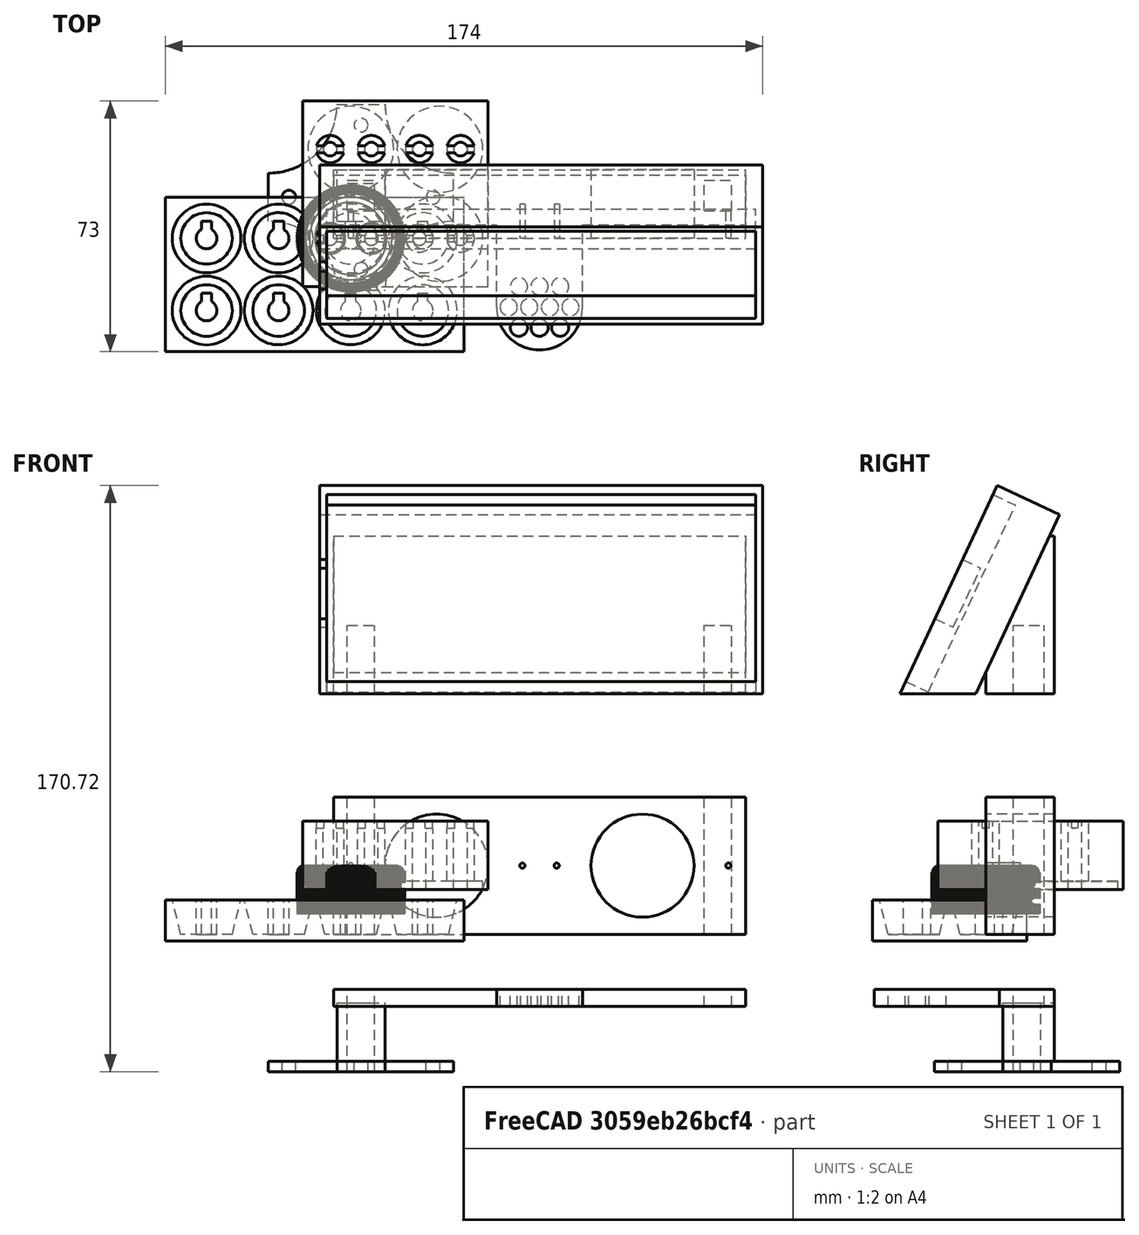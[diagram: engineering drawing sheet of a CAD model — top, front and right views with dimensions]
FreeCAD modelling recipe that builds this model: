
FCSTD DOCUMENT  (FreeCAD 0.14R3703 (Git))
Label: Drinks
License: CC-BY 3.0
LicenseURL: http://creativecommons.org/licenses/by/3.0/
objects: Part::Cylinder×32, Part::Box×22, Part::Cut×21, Part::MultiFuse×19, Part::Feature×2, Part::Cone×1, Mesh::Feature×1
note: 97 computed .brp shape members not serialized (recipe doc carries the construction recipe); baked Part::Feature solids carry a one-line shape summary decoded from their .brp

FEATURE [Part::Box] Box  label="Cube"
  Height = 40
  Length = 120
  Placement = pos=(-5,0,0) rot=(0,0,1;0rad)
  Width = 20
FEATURE [Part::Cylinder] Cylinder  label="Zylinder"
  Angle = 360
  Height = 20
  Placement = pos=(25,20,20) rot=(1,0,0;1.5708rad)
  Radius = 15
FEATURE [Part::Cylinder] Cylinder001  label="Zylinder001"
  Angle = 360
  Height = 10
  Placement = pos=(0,10,20) rot=(1,0,0;1.5708rad)
  Radius = 0.75
FEATURE [Part::Cylinder] Cylinder002  label="Zylinder002"
  Angle = 360
  Height = 10
  Placement = pos=(50,10,20) rot=(1,0,0;1.5708rad)
  Radius = 0.75
FEATURE [Part::MultiFuse] Fusion
  Placement = pos=(60,0,0) rot=(0,0,1;0rad)
  Shapes = -> [Cylinder,Cylinder001,Cylinder002]
FEATURE [Part::MultiFuse] Fusion001
  Shapes = -> [Cylinder,Cylinder001,Cylinder002]
FEATURE [Part::Box] Box001  label="Cube001"
  Height = 40
  Length = 8
  Placement = pos=(-1,8,0) rot=(0,0,1;0rad)
  Width = 9
FEATURE [Part::Box] Box002  label="Cube002"
  Height = 40
  Length = 8
  Placement = pos=(103,8,0) rot=(0,0,1;0rad)
  Width = 9
FEATURE [Part::MultiFuse] Fusion002
  Shapes = -> [Fusion,Fusion001,Box001,Box002]
FEATURE [Part::Cut] Cut  label="MotorHalterung"
  Base = -> Box
  Tool = -> Fusion002
FEATURE [Part::Box] Box003  label="Cube003"
  Height = 67
  Length = 129
  Placement = pos=(-9,-25,70) rot=(-1,0,0;0.436332rad)
  Width = 20
FEATURE [Part::Box] Box004  label="Cube004"
  Height = 20
  Length = 8
  Placement = pos=(-1,8,70) rot=(0,0,1;0rad)
  Width = 9
FEATURE [Part::Box] Box005  label="Cube005"
  Height = 20
  Length = 8
  Placement = pos=(103,8,70) rot=(0,0,1;0rad)
  Width = 9
FEATURE [Part::Box] Box006  label="Cube006"
  Height = 46
  Length = 120
  Placement = pos=(-5,0,70) rot=(0,0,1;0rad)
  Width = 20
FEATURE [Part::Box] Box007  label="Cube007"
  Height = 60
  Length = 125
  Placement = pos=(-7,-24,74) rot=(-1,0,0;0.436332rad)
  Width = 8
FEATURE [Part::Box] Box008  label="Cube008"
  Height = 10
  Length = 129
  Placement = pos=(-9,-27,60) rot=(0,0,1;0rad)
  Width = 47
FEATURE [Part::MultiFuse] Fusion003
  Shapes = -> [Box003,Box006]
FEATURE [Part::MultiFuse] Fusion004
  Shapes = -> [Box004,Box005,Box007,Box008]
FEATURE [Part::Cut] Cut001
  Base = -> Fusion003
  Tool = -> Fusion004
FEATURE [Part::Box] Box009  label="Cube009"
  Height = 19
  Length = 2
  Placement = pos=(-9,-15,92) rot=(-1,0,0;0.436332rad)
  Width = 6
FEATURE [Part::Cut] Cut002  label="iPhoneHalterung"
  Base = -> Cut001
  Tool = -> Box009
FEATURE [Part::Box] Box010  label="Cube010"
  Height = 5
  Length = 8
  Placement = pos=(103,8,0) rot=(0,0,1;0rad)
  Width = 9
FEATURE [Part::Box] Box011  label="Cube011"
  Height = 5
  Length = 8
  Placement = pos=(-1,8,0) rot=(0,0,1;0rad)
  Width = 9
FEATURE [Part::Box] Box012  label="Cube012"
  Height = 5
  Length = 120
  Placement = pos=(-5,4,0) rot=(0,0,1;0rad)
  Width = 16
FEATURE [Part::Cylinder] Cylinder003  label="Zylinder003"
  Angle = 360
  Height = 5
  Placement = pos=(3,0,0) rot=(0,0,1;0rad)
  Radius = 2.5
FEATURE [Part::Cylinder] Cylinder004  label="Zylinder004"
  Angle = 360
  Height = 5
  Placement = pos=(9,0,0) rot=(0,0,1;0rad)
  Radius = 2.5
FEATURE [Part::Cylinder] Cylinder005  label="Zylinder005"
  Angle = 360
  Height = 5
  Placement = pos=(-3,0,0) rot=(0,0,1;0rad)
  Radius = 2.5
FEATURE [Part::Cylinder] Cylinder006  label="Zylinder006"
  Angle = 360
  Height = 5
  Placement = pos=(-9,0,0) rot=(0,0,1;0rad)
  Radius = 2.5
FEATURE [Part::Cylinder] Cylinder007  label="Zylinder007"
  Angle = 360
  Height = 5
  Placement = pos=(-6,6,0) rot=(0,0,1;0rad)
  Radius = 2.5
FEATURE [Part::Cylinder] Cylinder008  label="Zylinder008"
  Angle = 360
  Height = 5
  Placement = pos=(0,6,0) rot=(0,0,1;0rad)
  Radius = 2.5
FEATURE [Part::Cylinder] Cylinder009  label="Zylinder009"
  Angle = 360
  Height = 5
  Placement = pos=(0,-6,0) rot=(0,0,1;0rad)
  Radius = 2.5
FEATURE [Part::Cylinder] Cylinder010  label="Zylinder010"
  Angle = 360
  Height = 5
  Placement = pos=(-6,-6,0) rot=(0,0,1;0rad)
  Radius = 2.5
FEATURE [Part::Cylinder] Cylinder011  label="Zylinder011"
  Angle = 360
  Height = 5
  Placement = pos=(55,-20,0) rot=(0,0,1;0rad)
  Radius = 12.5
FEATURE [Part::Cylinder] Cylinder012  label="Zylinder012"
  Angle = 360
  Height = 5
  Placement = pos=(6,-6,0) rot=(0,0,1;0rad)
  Radius = 2.5
FEATURE [Part::Cylinder] Cylinder013  label="Zylinder013"
  Angle = 360
  Height = 5
  Placement = pos=(6,6,0) rot=(0,0,1;0rad)
  Radius = 2.5
FEATURE [Part::MultiFuse] Fusion005
  Placement = pos=(55,-20,0) rot=(0,0,1;0rad)
  Shapes = -> [Cylinder013,Cylinder012,Cylinder010,Cylinder009,Cylinder008,Cylinder005,Cylinder003,Cylinder004,Cylinder006,Cylinder007]
FEATURE [Part::Box] Box013  label="Cube013"
  Height = 5
  Length = 25
  Placement = pos=(42.5,-20,0) rot=(0,0,1;0rad)
  Width = 26
FEATURE [Part::MultiFuse] Fusion006
  Shapes = -> [Box012,Box013,Cylinder011]
FEATURE [Part::MultiFuse] Fusion007
  Shapes = -> [Fusion005,Box010,Box011]
FEATURE [Part::Cut] Cut003  label="SchlauchHalterung"
  Base = -> Fusion006
  Placement = pos=(0,0,-21) rot=(0,0,1;0rad)
  Tool = -> Fusion007
FEATURE [Part::Box] Box015  label="Cube015"
  Height = 20
  Length = 14
  Placement = pos=(-4,5,-40) rot=(0,0,1;0rad)
  Width = 15
FEATURE [Part::Box] Box016  label="Cube016"
  Height = 20
  Length = 8
  Placement = pos=(-1,8,-40) rot=(0,0,1;0rad)
  Width = 8
FEATURE [Part::Box] Box018  label="Cube018"
  Height = 3
  Length = 54
  Placement = pos=(-24,-15,-40) rot=(0,0,1;0rad)
  Width = 54
FEATURE [Part::Cylinder] Cylinder014  label="Zylinder014"
  Angle = 360
  Height = 3
  Placement = pos=(30,-15,-40) rot=(0,0,1;0rad)
  Radius = 20
FEATURE [Part::Cylinder] Cylinder015  label="Zylinder015"
  Angle = 360
  Height = 3
  Placement = pos=(-24,-15,-40) rot=(0,0,1;0rad)
  Radius = 20
FEATURE [Part::Cylinder] Cylinder016  label="Zylinder016"
  Angle = 360
  Height = 3
  Placement = pos=(-24,39,-40) rot=(0,0,1;0rad)
  Radius = 20
FEATURE [Part::Cylinder] Cylinder017  label="Zylinder017"
  Angle = 360
  Height = 3
  Placement = pos=(30,39,-40) rot=(0,0,1;0rad)
  Radius = 20
FEATURE [Part::Cylinder] Cylinder018  label="Zylinder018"
  Angle = 360
  Height = 3
  Placement = pos=(3,-9,-40) rot=(0,0,1;0rad)
  Radius = 2
FEATURE [Part::Cylinder] Cylinder019  label="Zylinder019"
  Angle = 360
  Height = 3
  Placement = pos=(3,33,-40) rot=(0,0,1;0rad)
  Radius = 2
FEATURE [Part::Cylinder] Cylinder020  label="Zylinder020"
  Angle = 360
  Height = 3
  Placement = pos=(24,12,-40) rot=(0,0,1;0rad)
  Radius = 2
FEATURE [Part::Cylinder] Cylinder021  label="Zylinder021"
  Angle = 360
  Height = 3
  Placement = pos=(-18,12,-40) rot=(0,0,1;0rad)
  Radius = 2
FEATURE [Part::MultiFuse] Fusion008
  Shapes = -> [Box015,Box018]
FEATURE [Part::MultiFuse] Fusion009
  Shapes = -> [Box016,Cylinder018,Cylinder019,Cylinder014,Cylinder021,Cylinder017,Cylinder016,Cylinder015,Cylinder020]
FEATURE [Part::Cut] Cut004  label="Sockel"
  Base = -> Fusion008
  Tool = -> Fusion009
FEATURE [Part::Cone] Cone  label="Kegel"
  Angle = 360
  Height = 10
  Radius1 = 7.5
  Radius2 = 10
FEATURE [Part::Cylinder] Cylinder022  label="Zylinder022"
  Angle = 360
  Height = 10
  Radius = 3
FEATURE [Part::Box] Box019  label="Cube019"
  Height = 10
  Length = 3
  Placement = pos=(-1.5,2,0) rot=(0,0,1;0rad)
  Width = 3
FEATURE [Part::MultiFuse] Fusion010
  Shapes = -> [Cylinder022,Box019]
FEATURE [Part::Cut] Cut005
  Base = -> Cone
  Placement = pos=(21,-21,0) rot=(0,0,1;0rad)
  Tool = -> Fusion010
FEATURE [Part::Cut] Cut006
  Base = -> Cone
  Placement = pos=(0,-21,0) rot=(0,0,1;0rad)
  Tool = -> Fusion010
FEATURE [Part::Cut] Cut007
  Base = -> Cone
  Placement = pos=(-42,-21,0) rot=(0,0,1;0rad)
  Tool = -> Fusion010
FEATURE [Part::Cut] Cut008
  Base = -> Cone
  Placement = pos=(21,0,0) rot=(0,0,1;0rad)
  Tool = -> Fusion010
FEATURE [Part::Cut] Cut009
  Base = -> Cone
  Placement = pos=(-42,0,0) rot=(0,0,1;0rad)
  Tool = -> Fusion010
FEATURE [Part::Cut] Cut010
  Base = -> Cone
  Tool = -> Fusion010
FEATURE [Part::Cut] Cut011
  Base = -> Cone
  Placement = pos=(-21,-21,0) rot=(0,0,1;0rad)
  Tool = -> Fusion010
FEATURE [Part::Cut] Cut012
  Base = -> Cone
  Placement = pos=(-21,0,0) rot=(0,0,1;0rad)
  Tool = -> Fusion010
FEATURE [Part::Box] Box020  label="Cube020"
  Height = 12
  Length = 87
  Placement = pos=(-54,-33,-2) rot=(0,0,1;0rad)
  Width = 45
FEATURE [Part::MultiFuse] Fusion011
  Shapes = -> [Cut005,Cut006,Cut007,Cut008,Cut009,Cut010,Cut011,Cut012]
FEATURE [Part::Cut] Cut013  label="zapfen"
  Base = -> Box020
  Tool = -> Fusion011
FEATURE [Mesh::Feature] pco28cap_o
FEATURE [Part::Cylinder] Cylinder023  label="Zylinder023"
  Angle = 360
  Height = 20
  Placement = pos=(6,0,13) rot=(0,0,1;0rad)
  Radius = 4
FEATURE [Part::Cylinder] Cylinder024  label="Zylinder024"
  Angle = 360
  Height = 20
  Placement = pos=(-6,0,13) rot=(0,0,1;0rad)
  Radius = 4
FEATURE [Part::MultiFuse] Fusion012
  Shapes = -> [Cylinder024,Cylinder023]
FEATURE [Part::Cylinder] Cylinder025  label="Zylinder025"
  Angle = 360
  Height = 20
  Placement = pos=(-6,0,13) rot=(0,0,1;0rad)
  Radius = 2
FEATURE [Part::Cylinder] Cylinder026  label="Zylinder026"
  Angle = 360
  Height = 20
  Placement = pos=(6,0,13) rot=(0,0,1;0rad)
  Radius = 2
FEATURE [Part::MultiFuse] Fusion013
  Shapes = -> [Cylinder025,Cylinder026]
FEATURE [Part::Cylinder] Cylinder027  label="Zylinder027"
  Angle = 360
  Height = 2.5
  Placement = pos=(0,0,13) rot=(0,0,1;0rad)
  Radius = 12.5
FEATURE [Part::MultiFuse] Fusion014
  Shapes = -> [Fusion012,Cylinder027]
FEATURE [Part::Cut] Cut014
  Base = -> Fusion014
  Placement = pos=(0,26,0) rot=(0,0,1;0rad)
  Tool = -> Fusion013
FEATURE [Part::Cut] Cut015
  Base = -> Fusion014
  Placement = pos=(26,26,0) rot=(0,0,1;0rad)
  Tool = -> Fusion013
FEATURE [Part::Cut] Cut016
  Base = -> Fusion014
  Tool = -> Fusion013
FEATURE [Part::Cut] Cut017
  Base = -> Fusion014
  Placement = pos=(26,0,0) rot=(0,0,1;0rad)
  Tool = -> Fusion013
FEATURE [Part::Box] Box021  label="Cube021"
  Height = 20
  Length = 54
  Placement = pos=(-14,-14,13) rot=(0,0,1;0rad)
  Width = 54
FEATURE [Part::MultiFuse] Fusion015
  Shapes = -> [Cut014,Cut016,Cut017,Cut015]
FEATURE [Part::Cut] Cut018  label="DichtungsForm"
  Base = -> Box021
  Tool = -> Fusion015
FEATURE [Part::Box] Box022  label="Cube022"
  Height = 2
  Length = 47
  Placement = pos=(-10,-1,31) rot=(0,0,1;0rad)
  Width = 2
FEATURE [Part::Box] Box023  label="Cube023"
  Height = 2
  Length = 47
  Placement = pos=(-10,25,31) rot=(0,0,1;0rad)
  Width = 2
FEATURE [Part::MultiFuse] Fusion016  label="Dichtungen"
  Shapes = -> [Cut018,Box022,Box023]
FEATURE [Part::Cylinder] Cylinder028  label="Zylinder028"
  Angle = 360
  Height = 10
  Placement = pos=(-6,0,16) rot=(0,0,1;0rad)
  Radius = 4.5
FEATURE [Part::Feature] pco28cap_o001
  shape: bbox 31.4 x 31.4 x 14 mm, 27678 faces, 0 solids (baked)
FEATURE [Part::Feature] pco28cap_o001_solid  label="pco28cap_o001 (Solid)"
  shape: bbox 31.4 x 31.4 x 14 mm, 27678 faces (baked)
FEATURE [Part::Cylinder] Cylinder029  label="Zylinder029"
  Angle = 360
  Height = 10
  Placement = pos=(6,0,16) rot=(0,0,1;0rad)
  Radius = 4.5
FEATURE [Part::MultiFuse] Fusion017
  Shapes = -> [Cylinder028,Cylinder029]
FEATURE [Part::Cut] Cut019
  Base = -> pco28cap_o001_solid
  Tool = -> Fusion017
FEATURE [Part::Cylinder] Cylinder030  label="Zylinder030"
  Angle = 360
  Height = 3.5
  Radius = 10.5
FEATURE [Part::Cylinder] Cylinder031  label="Zylinder031"
  Angle = 360
  Height = 3.5
  Radius = 12
FEATURE [Part::Cut] Cut020
  Base = -> Cylinder031
  Placement = pos=(0,0,16.2) rot=(0,0,1;0rad)
  Tool = -> Cylinder030
FEATURE [Part::MultiFuse] Fusion018  label="Deckel"
  Shapes = -> [Cut019,Cut020]
